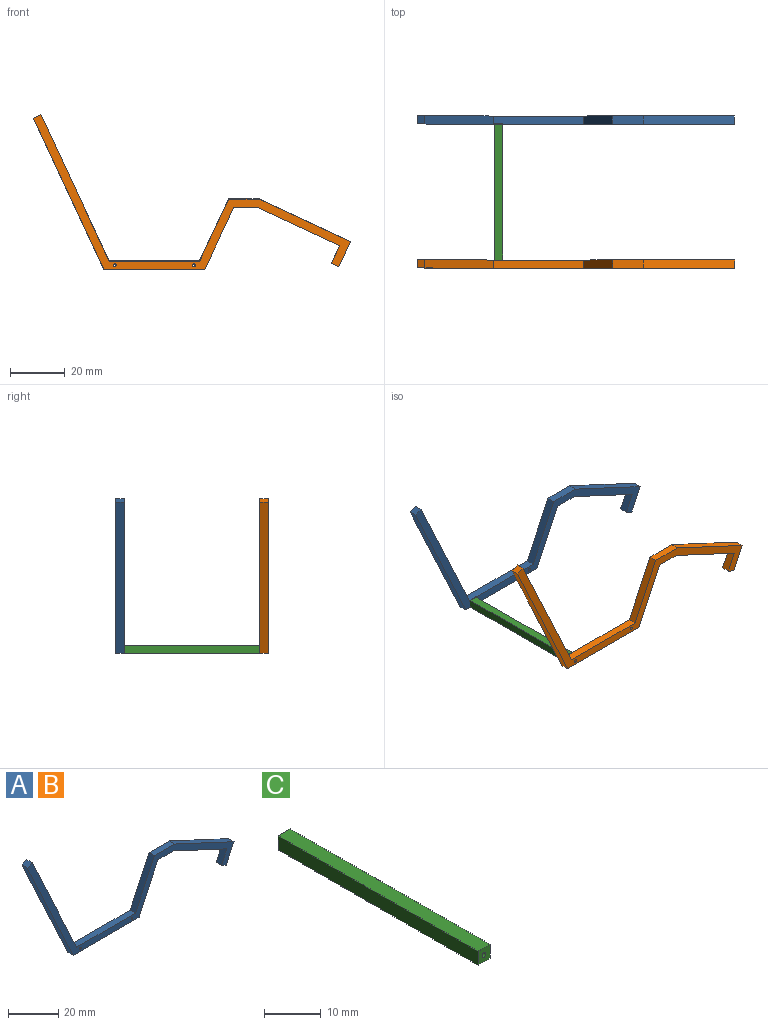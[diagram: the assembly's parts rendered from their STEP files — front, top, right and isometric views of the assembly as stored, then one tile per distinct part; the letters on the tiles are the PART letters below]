
ASSEMBLY  parts=3 mates=1
PART A: 18 faces, bbox 116x3x56.5 mm
  f0: plane 3x2.73mm, normal (-0.42,0,-0.91), area 9.1mm2, adj f2,f3,f13,f15
  f1: plane 3x2.73mm, normal (-0.42,0,0.91), area 9.1mm2, adj f12,f13,f14,f15
  f2: plane 9.23x4.31mm, normal (0.91,0,-0.42), area 30.6mm2, adj f0,f5,f13,f15
  f3: plane 6.5x3.03mm, normal (-0.91,0,0.42), area 21.5mm2, adj f0,f4,f13,f15
  f4: plane 30.05x14.01mm, normal (-0.42,0,-0.91), area 99.5mm2, adj f3,f6,f13,f15
  f5: plane 33.39x15.57mm, normal (0.42,0,0.91), area 110.5mm2, adj f2,f7,f13,f15
  f6: plane 8.7x3mm, normal (0,0,-1), area 26.1mm2, adj f4,f8,f13,f15
  f7: plane 11.3x3mm, normal (0,0,1), area 33.9mm2, adj f5,f9,f13,f15
  f8: plane 22.66x10.57mm, normal (0.91,0,-0.42), area 75mm2, adj f6,f10,f13,f15
  f9: plane 22.66x10.57mm, normal (-0.91,0,0.42), area 75mm2, adj f7,f11,f13,f15
  f10: plane 36.92x3mm, normal (0,0,-1), area 110.8mm2, adj f8,f12,f13,f15
  f11: plane 33.08x3mm, normal (0,0,1), area 99.2mm2, adj f9,f13,f14,f15
  f12: plane 55.25x25.76mm, normal (-0.91,0,-0.42), area 182.9mm2, adj f1,f10,f13,f15
  f13: plane 116.02x56.52mm, normal (0,-1,0), area 522.4mm2, adj f0,f1,f2,f3,f4,f5,f6,f7
  f14: plane 53.51x24.95mm, normal (0.91,0,0.42), area 177.1mm2, adj f1,f11,f13,f15
  f15: plane 116.02x56.52mm, normal (0,1,0), area 522.4mm2, adj f0,f1,f2,f3,f4,f5,f6,f7
  f16: cylinder r=0.51mm len=3mm, axis (0,-1,0), area 9.6mm2, adj f13,f15
  f17: cylinder r=0.5mm len=3mm, axis (0,-1,0), area 9.4mm2, adj f13,f15
PART B: same geometry as A
PART C: 7 faces, bbox 3x50x3 mm
  f0: plane 50x3mm, normal (0,0,-1), area 150mm2, adj f1,f4,f5,f6
  f1: plane 50x3mm, normal (1,0,0), area 150mm2, adj f0,f2,f5,f6
  f2: plane 50x3mm, normal (0,0,1), area 150mm2, adj f1,f4,f5,f6
  f3: cylinder r=0.5mm len=50mm, axis (0,1,0), area 157.1mm2, adj f5,f6
  f4: plane 50x3mm, normal (-1,0,0), area 150mm2, adj f0,f2,f5,f6
  f5: plane 3x3mm, normal (0,-1,0), area 8.2mm2, adj f0,f1,f2,f3,f4
  f6: plane 3x3mm, normal (0,1,0), area 8.2mm2, adj f0,f1,f2,f3,f4
PLACE A t=(-7.3,32.7,23.84)mm
PLACE B t=(-7.24,-19.98,23.78)mm
PLACE C t=(-4.24,31.52,23.78)mm
MATE fastened B.f17 <-> C.f3  axis (0,1,0) through (-4.24,-18.48,23.78)mm
